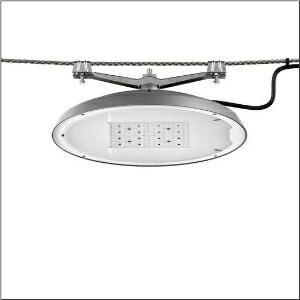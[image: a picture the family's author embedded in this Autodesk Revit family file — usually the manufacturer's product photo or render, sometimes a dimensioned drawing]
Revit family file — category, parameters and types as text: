
# Revit family: dl_50_iq_mini___st1_0s_5xa248w41f08le_b193
name_source: partatom
category: Lighting Fixtures
units: mm (PartAtom-declared; Revit-internal decimal feet)

## family parameters
Cut with Voids When Loaded = No
Host = Face
Light Source = No
Part Type = Normal
Room Calculation Point = No
Round Connector Dimension = Use Diameter
Shared = No

## types (1)
- --- (1 x LED, 10390 lm, 64.1 W, 4000K)
    Apparent Load = 64 VA
    CIE Flux Codes = 37 72 97 100 100
    Color Rendering = 70
    Color Temperature = 4000K
    Default Elevation = 1800 mm
    Description = DL 50 iQ mini, catenary luminaire, primary light control with lens, of PMMA, primary optical cover: cover, of toughened safety glass, transparent, light distribution: ST1.0s, light emission: direct distribution, primary light characteristic: symmetric, installation type: suspended mounting, LED, High Power LED, rated luminous flux: 10.390lm, luminous efficacy: 162lm/W, light colour: 740, colour temperature: 4000K, control gear: iQ Street-Remote, control: optimised constant luminous flux control (CLO 2.0), Desk-Remote (wireless, voltage-free reading and setting of iQ features in the workshop via application-optimized NFC function/RFID function), Light-Fading, Smart-Wire, Night-Set, Lumen-Switch, Temp-Guard, Auto-Match, Street-Remote, mains connection: 230..240V, AC, 50/60Hz, start of lifetime: 64W, end of service life: 67W, reduction: 30W, luminaire housing, of diecast aluminium, powder-coated, SITECO metallic grey (DB 702S), diameter: 500mm, height: 115mm, mounting height: 4..12m, protection rating (complete): IP66, insulation class (complete): insulation class II (safety insulation), certification: CE, ENEC, ENEC+, VDE, impact resistance: IK08, permissible operating ambient temperature for outdoor applications: -25..+40°C, standard-compliant lighting for roads and squares, packaging unit: 1 piece

Light Distribution: ST1.0s
    Height = 124 mm  [stored 0.406824 ft]
    Lamp = 1 x LED
    Lamp Light Flux = 10390 lm
    Lamp Power = 64.1 W
    Lamp count = 1
    Length = 500 mm
    Luminous efficacy = 162 lm/W
    Manufacturer = Siteco
    ModVariant = No
    Model = 5XA248W41F08LE
    Number of Poles = 1
    OnlyDefault = Yes
    Power Factor = 1
    Product Name = DL 50 iQ mini | ST1.0s
    Product group = catenary luminaire
    ProductGroupID = 6300
    Protection Class = Protection class II
    Protection Degree = IP 66
    RLX_Detail_Level = 1
    RLX_Emergency_Light_Flux = 0 lm
    RLX_Emergency_Type = 0
    RLX_Emergency_Type_DB = No
    RlxData = <blob elided: 127197 chars, md5=9cdc4eb9>
    Socket = socket
    Standby Power = 0 W
    System Light Flux = 10390 lm
    System Power = 64 W
    Type Comments = factory setting: luminous flux: 100 % | dim-lin: 254 | 672 mA
    Type Image = l_1251783.jpg
    URL = http://relux.com
    VarID = @adj_139983
    Voltage = 0 V
    Weight = 0.00 kg
    Width = 0 mm  [stored 0 ft]

note: [stored X ft] marks values corroborated as IEEE doubles in the binary element streams (Revit-internal decimal feet)

## geometry (parser evidence)
native form markers: Blend x4, Sweep x15
no freeform markers — native parametric forms only
